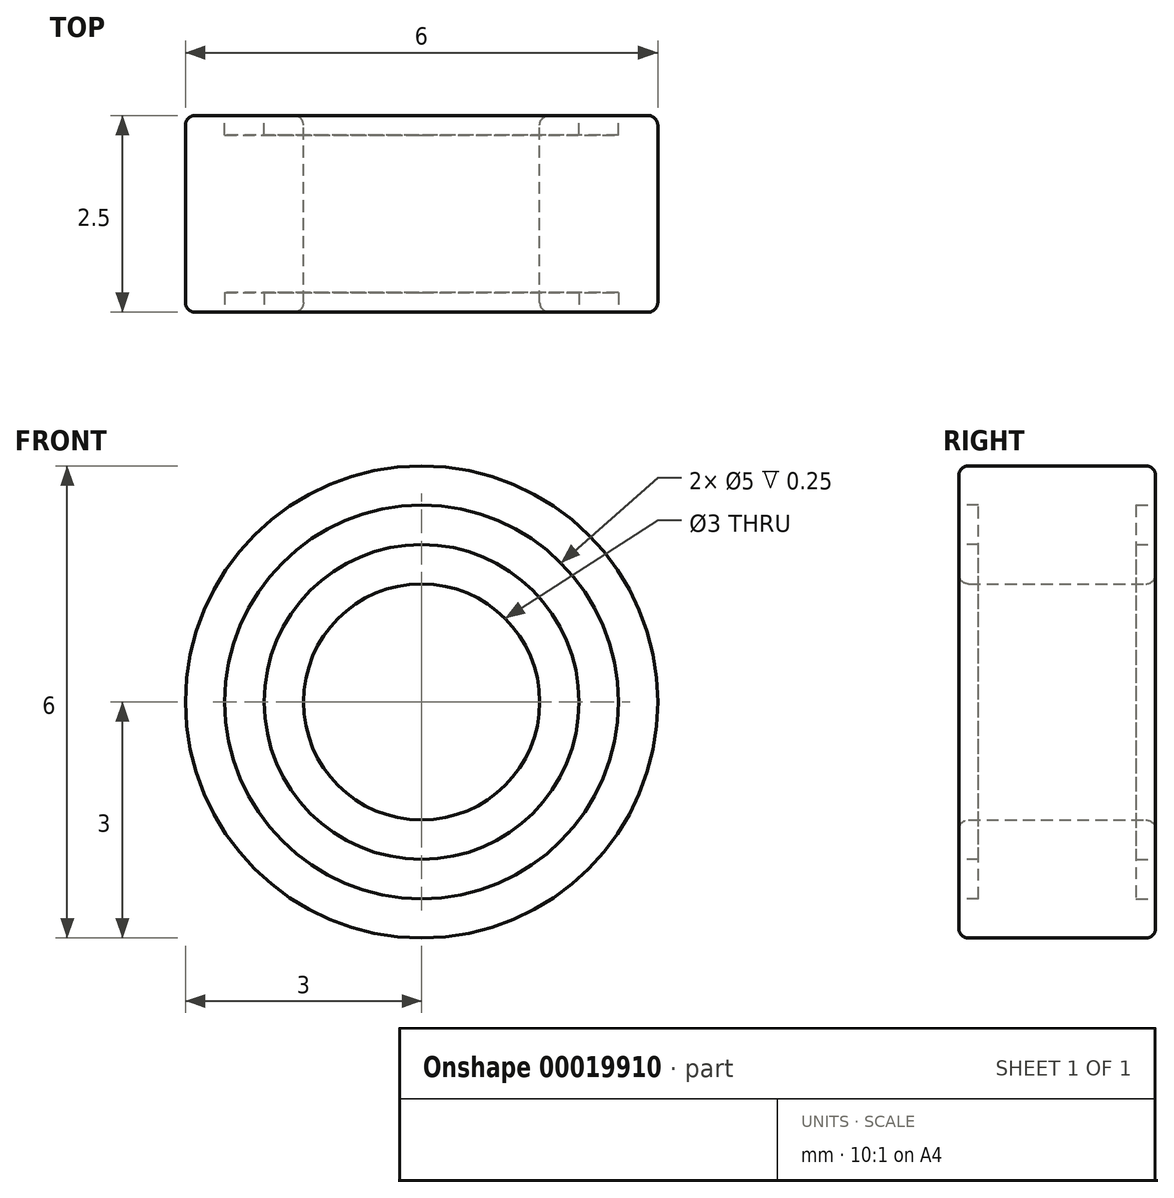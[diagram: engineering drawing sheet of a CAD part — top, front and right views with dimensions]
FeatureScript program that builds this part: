
annotation { "Feature Type Name" : "Feature", "Feature Type Description" : "" }
export const myFeature = defineFeature(function(context is Context, id is Id, definition is map)
    precondition{}
    {
        {
            var Q0;
            Q0=qCreatedBy(makeId("Front.planeOp"),FACE);
            var sketch = newSketch(context, id + "F0", { "sketchPlane" : qUnion([Q0])});
            skCircle(sketch, "E0", {"center": v(0, 0) * mm, "radius": 1.5 * mm});
            skCircle(sketch, "E1", {"center": v(0, 0) * mm, "radius": 3 * mm});
            skSolve(sketch);
        }
        {
            var Q0;
            Q0 = qSketchRegion(id + "F0", true);
            extrude(context, id + "F1", {"entities" : qUnion([Q0]), "depth" : 1.25 * mm, "hasSecondDirection" : true, "secondDirectionOppositeDirection" : true, "secondDirectionDepth" : 1.25 * mm});
        }
        {
            var Q0;
            Q0=makeQuery(id+"F1.opExtrude","CAP_FACE",FACE,{"disambiguationData":[OSD([sQuery(id+"F0.wireOp",EDGE,"E0"),sQuery(id+"F0.wireOp",EDGE,"E1")])],"isStart":false});
            var sketch = newSketch(context, id + "F2", { "sketchPlane" : qUnion([Q0])});
            skCircle(sketch, "E2", {"center": v(0, 0) * mm, "radius": 2 * mm});
            skCircle(sketch, "E3", {"center": v(0, 0) * mm, "radius": 2.5 * mm});
            skSolve(sketch);
        }
        {
            var Q0;
            Q0 = qSketchRegion(id + "F2", true);
            extrude(context, id + "F3", {"entities" : qUnion([Q0]), "operationType" : NewBodyOperationType.REMOVE, "oppositeDirection" : true, "depth" : .25 * mm});
        }
        {
            var Q0;
            Q0=makeQuery(id+"F1.opExtrude","CAP_FACE",FACE,{"disambiguationData":[OSD([sQuery(id+"F0.wireOp",EDGE,"E0"),sQuery(id+"F0.wireOp",EDGE,"E1")])],"isStart":true});
            var sketch = newSketch(context, id + "F4", { "sketchPlane" : qUnion([Q0])});
            skCircle(sketch, "E4", {"center": v(0, 0) * mm, "radius": 2 * mm});
            skCircle(sketch, "E5", {"center": v(0, 0) * mm, "radius": 2.5 * mm});
            skSolve(sketch);
        }
        {
            var Q0;
            Q0 = qSketchRegion(id + "F4", true);
            extrude(context, id + "F5", {"entities" : qUnion([Q0]), "operationType" : NewBodyOperationType.REMOVE, "oppositeDirection" : true, "depth" : .25 * mm});
        }
        {
            var Q0;
            Q0=makeQuery(id+"F1.opExtrude","CAP_EDGE",EDGE,{"disambiguationData":[OSD([sQuery(id+"F0.wireOp",EDGE,"E1")])],"isStart":true});
            var Q1;
            Q1=makeQuery(id+"F1.opExtrude","CAP_EDGE",EDGE,{"disambiguationData":[OSD([sQuery(id+"F0.wireOp",EDGE,"E1")])],"isStart":false});
            var Q2;
            Q2=makeQuery(id+"F1.opExtrude","CAP_EDGE",EDGE,{"disambiguationData":[OSD([sQuery(id+"F0.wireOp",EDGE,"E0")])],"isStart":true});
            var Q3;
            Q3=makeQuery(id+"F1.opExtrude","CAP_EDGE",EDGE,{"disambiguationData":[OSD([sQuery(id+"F0.wireOp",EDGE,"E0")])],"isStart":false});
            fillet(context, id + "F6", {"entities" : qUnion([Q0, Q1, Q2, Q3]), "radius" : .125 * mm, "tangentPropagation" : true, "allowEdgeOverflow" : false});
        }
    });
